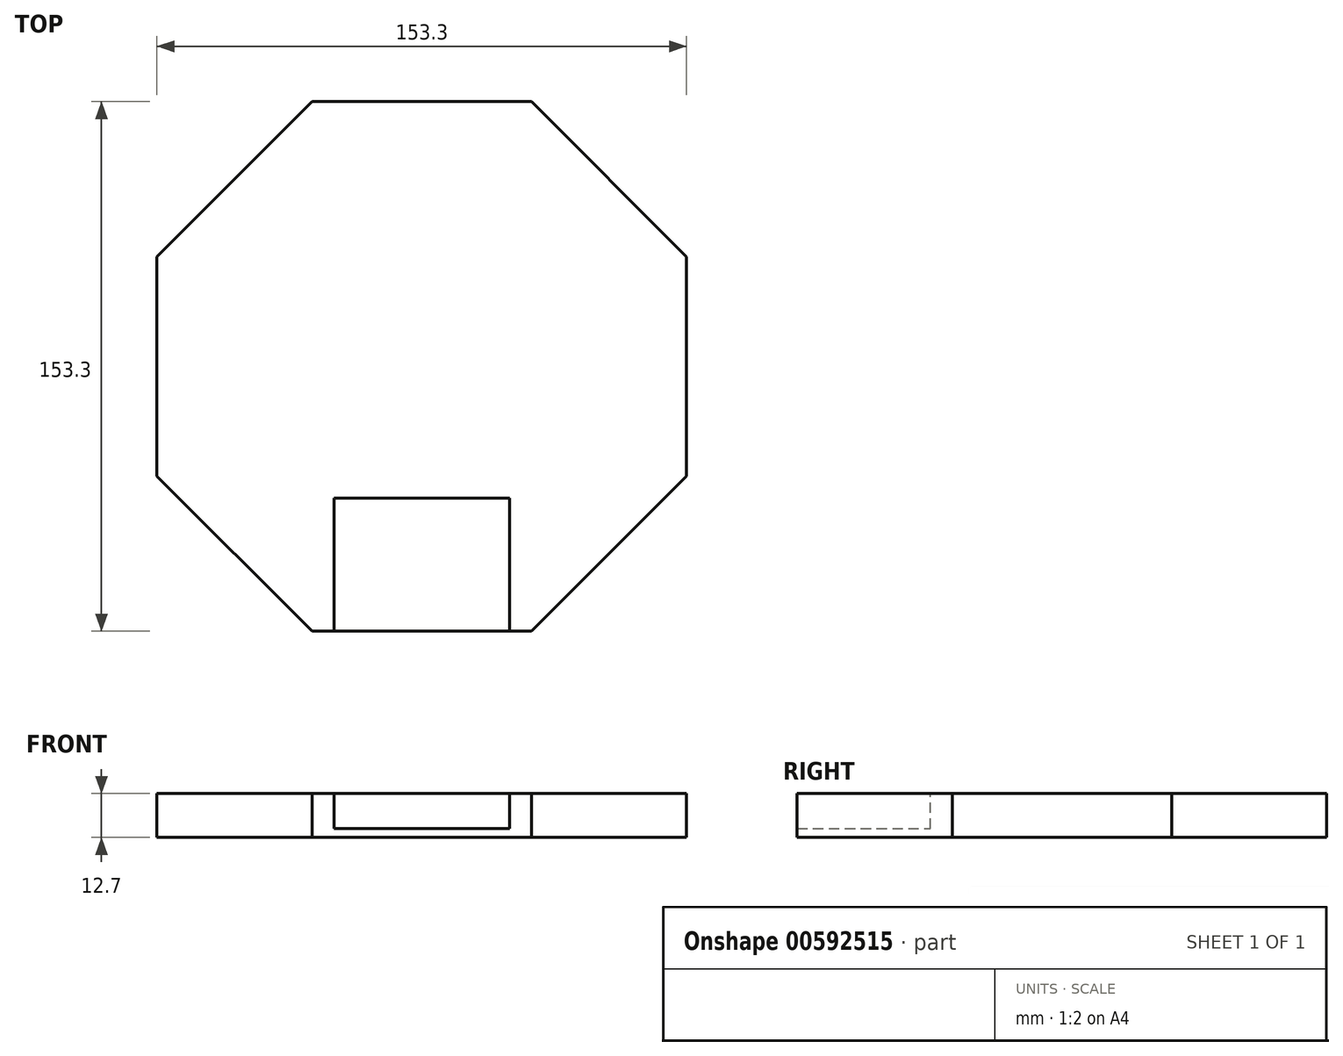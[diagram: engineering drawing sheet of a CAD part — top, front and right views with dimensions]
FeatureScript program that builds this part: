
annotation { "Feature Type Name" : "Feature", "Feature Type Description" : "" }
export const myFeature = defineFeature(function(context is Context, id is Id, definition is map)
    precondition{}
    {
        {
            var Q0;
            Q0=qCreatedBy(makeId("Top.planeOp"),FACE);
            var sketch = newSketch(context, id + "F0", { "sketchPlane" : qUnion([Q0])});
            skCircle(sketch, "E0.cCircle", {"center": v(0, 0) * mm, "radius": 76.65 * mm, "construction": true});
            skLineSegment(sketch, "E0.0", {"start": v(76.65, 31.75) * mm, "end": v(76.65, -31.75) * mm});
            skLineSegment(sketch, "E0.1", {"start": v(76.65, -31.75) * mm, "end": v(31.75, -76.65) * mm});
            skLineSegment(sketch, "E0.2", {"start": v(31.75, -76.65) * mm, "end": v(-31.75, -76.65) * mm});
            skLineSegment(sketch, "E0.3", {"start": v(-31.75, -76.65) * mm, "end": v(-76.65, -31.75) * mm});
            skLineSegment(sketch, "E0.4", {"start": v(-76.65, -31.75) * mm, "end": v(-76.65, 31.75) * mm});
            skLineSegment(sketch, "E0.5", {"start": v(-76.65, 31.75) * mm, "end": v(-31.75, 76.65) * mm});
            skLineSegment(sketch, "E0.6", {"start": v(-31.75, 76.65) * mm, "end": v(31.75, 76.65) * mm});
            skLineSegment(sketch, "E0.7", {"start": v(31.75, 76.65) * mm, "end": v(76.65, 31.75) * mm});
            skPoint(sketch, "E0.0.midPoint", {"position": v(76.65, 0) * mm});
            skSolve(sketch);
        }
        {
            var Q0;
            Q0=makeQuery(id+"F0.imprint","IMPRINT",FACE,{"disambiguationData":[TD([[makeQuery(id+"F0.imprint","IMPRINT",EDGE,{"derivedFrom":sQuery(id+"F0.wireOp",EDGE,"E0.0")}),-1.0]])]});
            extrude(context, id + "F1", {"entities" : qUnion([Q0]), "depth" : 12.7 * mm, "offsetDistance" : 25.4 * mm});
        }
        {
            var Q0;
            Q0=makeQuery(id+"F1.opExtrude","CAP_FACE",FACE,{"disambiguationData":[OSD([sQuery(id+"F0.wireOp",EDGE,"E0.0"),sQuery(id+"F0.wireOp",EDGE,"E0.1"),sQuery(id+"F0.wireOp",EDGE,"E0.2"),sQuery(id+"F0.wireOp",EDGE,"E0.3"),sQuery(id+"F0.wireOp",EDGE,"E0.4"),sQuery(id+"F0.wireOp",EDGE,"E0.5"),sQuery(id+"F0.wireOp",EDGE,"E0.6"),sQuery(id+"F0.wireOp",EDGE,"E0.7")])],"isStart":false});
            var sketch = newSketch(context, id + "F2", { "sketchPlane" : qUnion([Q0])});
            skLineSegment(sketch, "E1.bottom", {"start": v(-25.4, -76.65) * mm, "end": v(25.4, -76.65) * mm});
            skLineSegment(sketch, "E1.top", {"start": v(-25.4, -38.1) * mm, "end": v(25.4, -38.1) * mm});
            skLineSegment(sketch, "E1.left", {"start": v(-25.4, -76.65) * mm, "end": v(-25.4, -38.1) * mm});
            skLineSegment(sketch, "E1.right", {"start": v(25.4, -76.65) * mm, "end": v(25.4, -38.1) * mm});
            skSolve(sketch);
        }
        {
            var Q0;
            Q0=makeQuery(id+"F2.imprint","IMPRINT",FACE,{"disambiguationData":[TD([[makeQuery(id+"F2.imprint","IMPRINT",EDGE,{"derivedFrom":sQuery(id+"F2.wireOp",EDGE,"E1.bottom")}),-1.0]])]});
            extrude(context, id + "F3", {"entities" : qUnion([Q0]), "operationType" : NewBodyOperationType.REMOVE, "oppositeDirection" : true, "depth" : 10.16 * mm, "offsetDistance" : 25.4 * mm});
        }
    });
